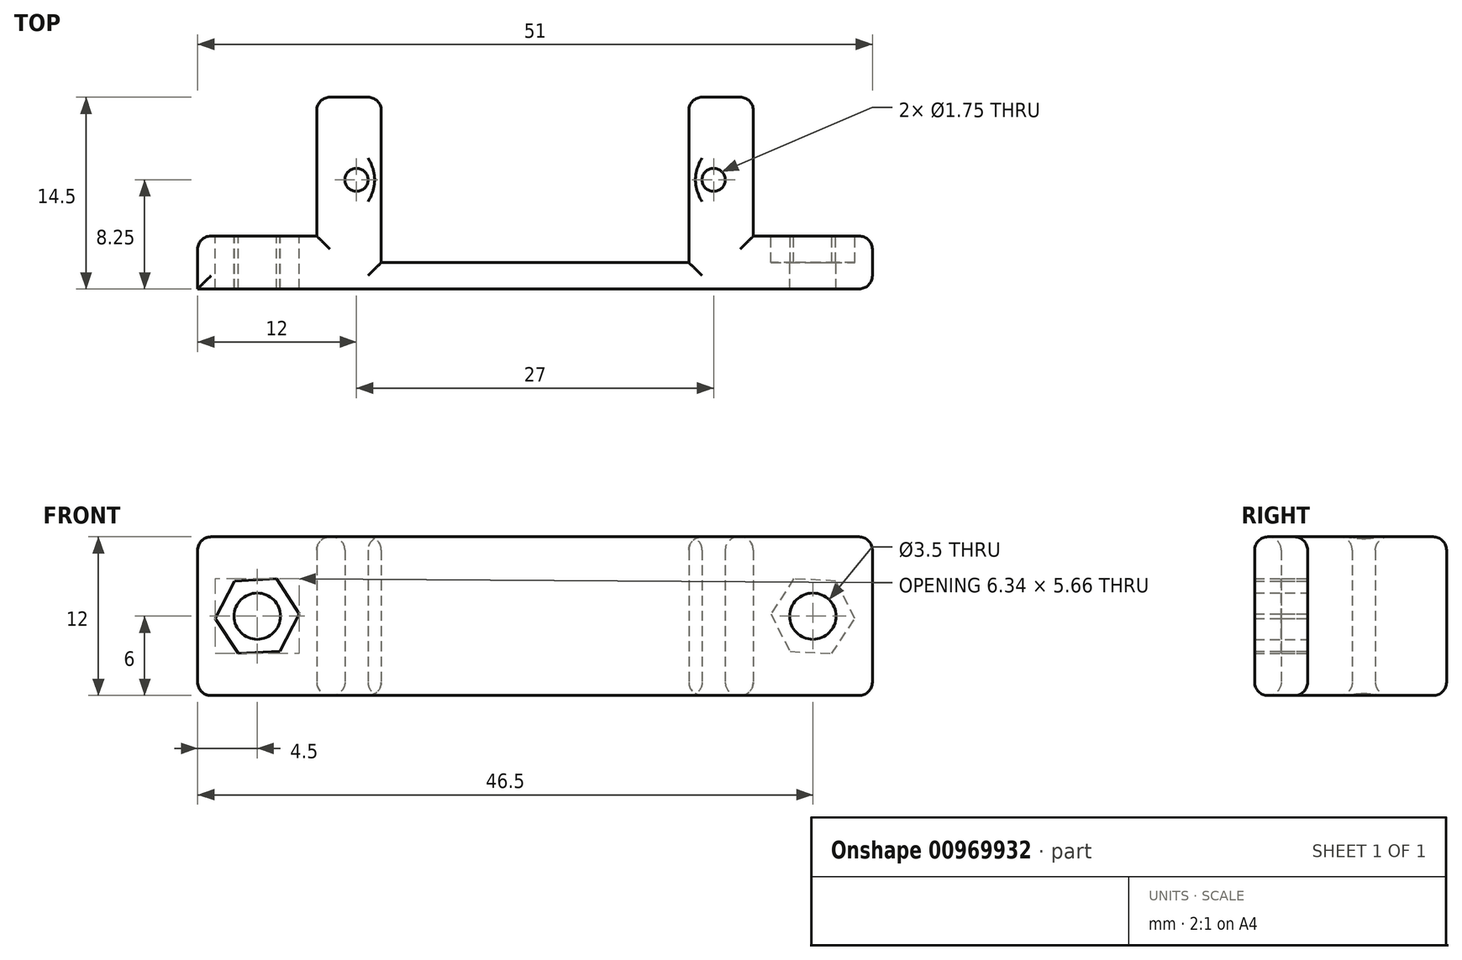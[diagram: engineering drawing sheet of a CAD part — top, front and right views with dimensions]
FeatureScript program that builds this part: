
annotation { "Feature Type Name" : "Feature", "Feature Type Description" : "" }
export const myFeature = defineFeature(function(context is Context, id is Id, definition is map)
    precondition{}
    {
        {
            var Q0;
            Q0=qCreatedBy(makeId("Top.planeOp"),FACE);
            var sketch = newSketch(context, id + "F0", { "sketchPlane" : qUnion([Q0])});
            skLineSegment(sketch, "E0.bottom", {"start": v(-16.5, 7.25) * mm, "end": v(16.5, 7.25) * mm});
            skLineSegment(sketch, "E0.top", {"start": v(-16.5, -7.25) * mm, "end": v(16.5, -7.25) * mm});
            skLineSegment(sketch, "E0.left", {"start": v(-16.5, 7.25) * mm, "end": v(-16.5, -7.25) * mm});
            skLineSegment(sketch, "E0.right", {"start": v(16.5, 7.25) * mm, "end": v(16.5, -7.25) * mm});
            skPoint(sketch, "E0.middle", {"position": v(0, 0) * mm});
            skLineSegment(sketch, "E1", {"start": v(-16.5, -5.25) * mm, "end": v(16.5, -5.25) * mm});
            skLineSegment(sketch, "E2", {"start": v(-11.62, 7.25) * mm, "end": v(-11.63, -5.25) * mm});
            skLineSegment(sketch, "E3.MirrorCS", {"start": v(11.62, 7.25) * mm, "end": v(11.63, -5.25) * mm});
            skCircle(sketch, "E4", {"center": v(-13.5, 1) * mm, "radius": 0.88 * mm});
            skCircle(sketch, "E5.MirrorC", {"center": v(13.5, 1) * mm, "radius": 0.88 * mm});
            skLineSegment(sketch, "E6.bottom", {"start": v(-16.5, -7.25) * mm, "end": v(-25.5, -7.25) * mm});
            skLineSegment(sketch, "E6.top", {"start": v(-16.5, -3.25) * mm, "end": v(-25.5, -3.25) * mm});
            skLineSegment(sketch, "E6.left", {"start": v(-16.5, -7.25) * mm, "end": v(-16.5, -3.25) * mm});
            skLineSegment(sketch, "E6.right", {"start": v(-25.5, -7.25) * mm, "end": v(-25.5, -3.25) * mm});
            skLineSegment(sketch, "E7.MirrorCS", {"start": v(16.5, -3.25) * mm, "end": v(25.5, -3.25) * mm});
            skLineSegment(sketch, "E8.MirrorCS", {"start": v(25.5, -7.25) * mm, "end": v(25.5, -3.25) * mm});
            skLineSegment(sketch, "E9.MirrorCS", {"start": v(16.5, -7.25) * mm, "end": v(25.5, -7.25) * mm});
            skSolve(sketch);
        }
        {
            var Q0;
            {var subQ3=sQuery(id+"F0.wireOp",EDGE,"E2");Q0=makeQuery(id+"F0.imprint","IMPRINT",FACE,{"disambiguationData":[TD([[makeQuery(id+"F0.imprint","IMPRINT",EDGE,{"derivedFrom":subQ3}),-1.0]])]});}
            var Q1;
            {var subQ1=sQuery(id+"F0.wireOp",EDGE,"E0.top");Q1=makeQuery(id+"F0.imprint","IMPRINT",FACE,{"disambiguationData":[TD([[makeQuery(id+"F0.imprint","IMPRINT",EDGE,{"derivedFrom":subQ1}),1.0]])]});}
            var Q2;
            {var subQ0=sQuery(id+"F0.wireOp",EDGE,"E7.MirrorCS");Q2=makeQuery(id+"F0.imprint","IMPRINT",FACE,{"disambiguationData":[TD([[makeQuery(id+"F0.imprint","IMPRINT",EDGE,{"derivedFrom":subQ0}),-1.0]])]});}
            var Q3;
            {var subQ4=sQuery(id+"F0.wireOp",EDGE,"E3.MirrorCS");Q3=makeQuery(id+"F0.imprint","IMPRINT",FACE,{"disambiguationData":[TD([[makeQuery(id+"F0.imprint","IMPRINT",EDGE,{"derivedFrom":subQ4}),1.0]])]});}
            var Q4;
            {var subQ1=sQuery(id+"F0.wireOp",EDGE,"E6.bottom");Q4=makeQuery(id+"F0.imprint","IMPRINT",FACE,{"disambiguationData":[TD([[makeQuery(id+"F0.imprint","IMPRINT",EDGE,{"derivedFrom":subQ1}),-1.0]])]});}
            extrude(context, id + "F1", {"entities" : qUnion([Q0, Q1, Q2, Q3, Q4]), "depth" : 12 * mm, "offsetDistance" : 25 * mm});
        }
        {
            var Q0;
            Q0=makeQuery(id+"F1.opExtrude","SWEPT_FACE",FACE,{"disambiguationData":[OSD([sQuery(id+"F0.wireOp",EDGE,"E7.MirrorCS")])]});
            var sketch = newSketch(context, id + "F2", { "sketchPlane" : qUnion([Q0])});
            skCircle(sketch, "E10.cCircle", {"center": v(-21, 6) * mm, "radius": 2.75 * mm, "construction": true});
            skLineSegment(sketch, "E10.0", {"start": v(-24.17, 5.84) * mm, "end": v(-22.73, 8.66) * mm});
            skLineSegment(sketch, "E10.1", {"start": v(-22.73, 8.66) * mm, "end": v(-19.56, 8.83) * mm});
            skLineSegment(sketch, "E10.2", {"start": v(-19.56, 8.83) * mm, "end": v(-17.83, 6.16) * mm});
            skLineSegment(sketch, "E10.3", {"start": v(-17.83, 6.16) * mm, "end": v(-19.27, 3.34) * mm});
            skLineSegment(sketch, "E10.4", {"start": v(-19.27, 3.34) * mm, "end": v(-22.44, 3.17) * mm});
            skLineSegment(sketch, "E10.5", {"start": v(-22.44, 3.17) * mm, "end": v(-24.17, 5.84) * mm});
            skPoint(sketch, "E10.0.midPoint", {"position": v(-23.45, 7.25) * mm});
            skCircle(sketch, "E11", {"center": v(-21, 6) * mm, "radius": 1.75 * mm});
            skLineSegment(sketch, "E12.MirrorCS", {"start": v(17.83, 6.16) * mm, "end": v(19.27, 3.34) * mm});
            skLineSegment(sketch, "E13.MirrorCS", {"start": v(22.44, 3.17) * mm, "end": v(24.17, 5.84) * mm});
            skLineSegment(sketch, "E14.MirrorCS", {"start": v(24.17, 5.84) * mm, "end": v(22.73, 8.66) * mm});
            skCircle(sketch, "E15.MirrorC", {"center": v(21, 6) * mm, "radius": 1.75 * mm});
            skLineSegment(sketch, "E16.MirrorCS", {"start": v(22.73, 8.66) * mm, "end": v(19.56, 8.83) * mm});
            skLineSegment(sketch, "E17.MirrorCS", {"start": v(19.27, 3.34) * mm, "end": v(22.44, 3.17) * mm});
            skCircle(sketch, "E18.MirrorC", {"center": v(21, 6) * mm, "radius": 2.75 * mm, "construction": true});
            skLineSegment(sketch, "E19.MirrorCS", {"start": v(19.56, 8.83) * mm, "end": v(17.83, 6.16) * mm});
            skPoint(sketch, "E20.MirrorP", {"position": v(23.45, 7.25) * mm});
            skSolve(sketch);
        }
        {
            var Q0;
            Q0=makeQuery(id+"F2.imprint","IMPRINT",FACE,{"disambiguationData":[TD([[makeQuery(id+"F2.imprint","IMPRINT",EDGE,{"derivedFrom":sQuery(id+"F2.wireOp",EDGE,"E11")}),1.0]])]});
            var Q1;
            Q1=makeQuery(id+"F2.imprint","IMPRINT",FACE,{"disambiguationData":[TD([[makeQuery(id+"F2.imprint","IMPRINT",EDGE,{"derivedFrom":sQuery(id+"F2.wireOp",EDGE,"E15.MirrorC")}),-1.0]])]});
            extrude(context, id + "F3", {"entities" : qUnion([Q0, Q1]), "operationType" : NewBodyOperationType.REMOVE, "oppositeDirection" : true, "depth" : 25 * mm, "offsetDistance" : 25 * mm});
        }
        {
            var Q0;
            Q0=makeQuery(id+"F2.imprint","IMPRINT",FACE,{"disambiguationData":[TD([[makeQuery(id+"F2.imprint","IMPRINT",EDGE,{"derivedFrom":sQuery(id+"F2.wireOp",EDGE,"E12.MirrorCS")}),1.0]])]});
            var Q1;
            Q1=makeQuery(id+"F2.imprint","IMPRINT",FACE,{"disambiguationData":[TD([[makeQuery(id+"F2.imprint","IMPRINT",EDGE,{"derivedFrom":sQuery(id+"F2.wireOp",EDGE,"E10.0")}),-1.0]])]});
            extrude(context, id + "F4", {"entities" : qUnion([Q0, Q1]), "operationType" : NewBodyOperationType.REMOVE, "oppositeDirection" : true, "depth" : 2 * mm, "offsetDistance" : 25 * mm});
        }
        {
            var Q0;
            Q0=makeQuery(id+"F1.opExtrude","SWEPT_EDGE",EDGE,{"disambiguationData":[OSD([sQuery(id+"F0.wireOp",EDGE,"E0.bottom"),sQuery(id+"F0.wireOp",EDGE,"E0.right")])]});
            var Q1;
            Q1=makeQuery(id+"F1.opExtrude","CAP_EDGE",EDGE,{"disambiguationData":[OSD([sQuery(id+"F0.wireOp",EDGE,"E3.MirrorCS")])],"isStart":true});
            var Q2;
            Q2=makeQuery(id+"F1.opExtrude","SWEPT_EDGE",EDGE,{"disambiguationData":[OSD([sQuery(id+"F0.wireOp",EDGE,"E0.bottom"),sQuery(id+"F0.wireOp",EDGE,"E3.MirrorCS")])]});
            var Q3;
            Q3=makeQuery(id+"F1.opExtrude","CAP_EDGE",EDGE,{"disambiguationData":[OSD([sQuery(id+"F0.wireOp",EDGE,"E0.right")])],"isStart":true});
            var Q4;
            Q4=makeQuery(id+"F1.opExtrude","SWEPT_EDGE",EDGE,{"disambiguationData":[OSD([sQuery(id+"F0.wireOp",EDGE,"E0.bottom"),sQuery(id+"F0.wireOp",EDGE,"E2")])]});
            var Q5;
            {var subQ0=sQuery(id+"F0.wireOp",EDGE,"E0.bottom");Q5=makeQuery(id+"F1.opExtrude","SWEPT_FACE",FACE,{"disambiguationData":[OSD([subQ0]),TDD([makeQuery(id+"F0.imprint","IMPRINT",EDGE,{"disambiguationData":[TD([[makeQuery(id+"F0.imprint","INTERSECT",VERTEX,{"derivedFrom":[subQ0,sQuery(id+"F0.wireOp",EDGE,"E2")]}),1.0]])],"derivedFrom":subQ0})])]});}
            var Q6;
            Q6=makeQuery(id+"F1.opExtrude","CAP_FACE",FACE,{"disambiguationData":[OSD([sQuery(id+"F0.wireOp",EDGE,"E0.bottom"),sQuery(id+"F0.wireOp",EDGE,"E0.top"),sQuery(id+"F0.wireOp",EDGE,"E0.left"),sQuery(id+"F0.wireOp",EDGE,"E0.right"),sQuery(id+"F0.wireOp",EDGE,"E1"),sQuery(id+"F0.wireOp",EDGE,"E2"),sQuery(id+"F0.wireOp",EDGE,"E3.MirrorCS"),sQuery(id+"F0.wireOp",EDGE,"E4"),sQuery(id+"F0.wireOp",EDGE,"E5.MirrorC"),sQuery(id+"F0.wireOp",EDGE,"E6.bottom"),sQuery(id+"F0.wireOp",EDGE,"E6.top"),sQuery(id+"F0.wireOp",EDGE,"E6.right"),sQuery(id+"F0.wireOp",EDGE,"E7.MirrorCS"),sQuery(id+"F0.wireOp",EDGE,"E8.MirrorCS"),sQuery(id+"F0.wireOp",EDGE,"E9.MirrorCS")])],"isStart":true});
            var Q7;
            Q7=makeQuery(id+"F1.opExtrude","SWEPT_EDGE",EDGE,{"disambiguationData":[OSD([sQuery(id+"F0.wireOp",EDGE,"E8.MirrorCS"),sQuery(id+"F0.wireOp",EDGE,"E9.MirrorCS")])]});
            var Q8;
            Q8=makeQuery(id+"F1.opExtrude","SWEPT_EDGE",EDGE,{"disambiguationData":[OSD([sQuery(id+"F0.wireOp",EDGE,"E7.MirrorCS"),sQuery(id+"F0.wireOp",EDGE,"E8.MirrorCS")])]});
            var Q9;
            Q9=makeQuery(id+"F1.opExtrude","CAP_EDGE",EDGE,{"disambiguationData":[OSD([sQuery(id+"F0.wireOp",EDGE,"E8.MirrorCS")])],"isStart":false});
            var Q10;
            Q10=makeQuery(id+"F1.opExtrude","CAP_FACE",FACE,{"disambiguationData":[OSD([sQuery(id+"F0.wireOp",EDGE,"E0.bottom"),sQuery(id+"F0.wireOp",EDGE,"E0.top"),sQuery(id+"F0.wireOp",EDGE,"E0.left"),sQuery(id+"F0.wireOp",EDGE,"E0.right"),sQuery(id+"F0.wireOp",EDGE,"E1"),sQuery(id+"F0.wireOp",EDGE,"E2"),sQuery(id+"F0.wireOp",EDGE,"E3.MirrorCS"),sQuery(id+"F0.wireOp",EDGE,"E4"),sQuery(id+"F0.wireOp",EDGE,"E5.MirrorC"),sQuery(id+"F0.wireOp",EDGE,"E6.bottom"),sQuery(id+"F0.wireOp",EDGE,"E6.top"),sQuery(id+"F0.wireOp",EDGE,"E6.right"),sQuery(id+"F0.wireOp",EDGE,"E7.MirrorCS"),sQuery(id+"F0.wireOp",EDGE,"E8.MirrorCS"),sQuery(id+"F0.wireOp",EDGE,"E9.MirrorCS")])],"isStart":false});
            var Q11;
            Q11=makeQuery(id+"F1.opExtrude","SWEPT_EDGE",EDGE,{"disambiguationData":[OSD([sQuery(id+"F0.wireOp",EDGE,"E6.top"),sQuery(id+"F0.wireOp",EDGE,"E6.right")])]});
            fillet(context, id + "F5", {"entities" : qUnion([Q0, Q1, Q2, Q3, Q4, Q5, Q6, Q7, Q8, Q9, Q10, Q11]), "radius" : 1 * mm, "tangentPropagation" : true, "allowEdgeOverflow" : false});
        }
    });
